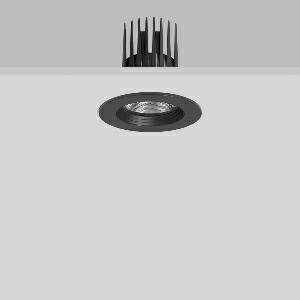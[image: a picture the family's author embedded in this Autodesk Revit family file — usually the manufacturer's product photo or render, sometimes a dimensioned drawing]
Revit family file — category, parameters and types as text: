
# Revit family: heledon_mini_e_901748_003_2_7838
name_source: partatom
category: Lighting Fixtures
units: mm (PartAtom-declared; Revit-internal decimal feet)

## family parameters
Cut with Voids When Loaded = No
Host = Face
Light Source = No
Part Type = Normal
Room Calculation Point = No
Round Connector Dimension = Use Diameter
Shared = No

## types (1)
- HELEDON mini E (1 x LED Modul 927, 3400 lm, 2700)
    Apparent Load = 29 VA
    Approval mark = CE
    CIE Flux Codes = 100 100 100 100 100
    Color Rendering = 92
    Color Temperature = 2700
    Default Elevation = 1800 mm
    Description = Series: HELEDON mini
Round recessed downlight. Housing: die-cast aluminium, powder-coated. Black plastic ring and recessed LED to prevent glare from the side. Optical assembly with reflector made of MIRO-Silver with 98% total light reflection for outstanding efficiency - can be changed without tools. Best colour rendering index Ra>90. Suitable for Recessed ceiling mounting. Installation without tools thanks to spring fastening system. Including separate LED converter with connecting cable 600 mm.High quality converter without flickering and stroboscopic effect. Through-wiring box (5 pole) available as accessory. The following accessories can be mounted without use of tools: interchangeable lenses, decorative glasses, honeycomb louvre, clear and frosted diffusers, white interchangeable plastic ring. 
Colour: deep black, matt (RAL 9005)
Diameter: 124 mm
Height: 3 mm
Cut-out diameter: 114 mm
Recess height: 170 mm
Luminaire: recess height: 120 mm
Lamp: LED
Socket: without socket
Colour temperature: 2700K
Colour rendering index (CRI): 92
System power: 29 W
Rated luminous flux: 3400 lm
Luminous efficiency: 117 lm/W
Control gear: Regulated power supply
Protection class: II
Type of protection: IP 20
    Height = 0 mm  [stored 0 ft]
    Lamp = 1 x LED Modul 927
    Lamp Light Flux = 3400 lm
    Lamp count = 1
    Length = 124 mm  [stored 0.406824 ft]
    Lifetime = 50000 h
    Luminous efficacy = 117 lm/W
    Manufacturer = RZB
    ModVariant = No
    Model = 901748.003.2
    Mounting Place = Ceiling
    Mounting Type = Recessed
    Number of Poles = 1
    OnlyDefault = Yes
    Power Factor = 1
    Product Name = HELEDON mini E
    Product group = Recessed downlights
    ProductGroupID = 402
    Protection Class = Protection class II
    Protection Degree = IP 20
    RLX_Detail_Level = 1
    RLX_Emergency_Light_Flux = 0 lm
    RLX_Emergency_Type = 0
    RLX_Emergency_Type_DB = No
    RlxData = <blob elided: 127405 chars, md5=16aab5a8>
    Socket = socket
    Standby Power = 0 W
    System Light Flux = 3400 lm
    System Power = 29 W
    Type Comments = Product without accessories
    Type Image = 901657.003.jpg
    URL = http://relux.com
    VarID = ---
    Voltage = 230 V
    Voltage Range = 220-240 V
    Weight = 0.00 kg
    Width = 0 mm  [stored 0 ft]

note: [stored X ft] marks values corroborated as IEEE doubles in the binary element streams (Revit-internal decimal feet)

## geometry (parser evidence)
native form markers: Blend x4, Sweep x13
no freeform markers — native parametric forms only
